FCSTD DOCUMENT  (FreeCAD 0.17R8360 (Git))
Label: cable_chain_sketch
License: All rights reserved
LicenseURL: http://de.wikipedia.org/wiki/Alle_Rechte_vorbehalten
objects: Sketcher::SketchObject×1
note: 1 computed .brp shape members not serialized (recipe doc carries the construction recipe); baked Part::Feature solids carry a one-line shape summary decoded from their .brp

FEATURE [Sketcher::SketchObject] sketch
  sketch-geometry (4):
    g0: ArcOfCircle CenterX=0 CenterY=0 CenterZ=0 NormalX=0 NormalY=0 NormalZ=1 Radius=2.5 StartAngle=1.5708 EndAngle=4.71239
    g1: ArcOfCircle CenterX=15 CenterY=0 CenterZ=0 NormalX=0 NormalY=0 NormalZ=1 Radius=2.5 StartAngle=4.71239 EndAngle=7.85398
    g2: LineSegment StartX=-7.07e-09 StartY=2.5 StartZ=0 EndX=15 EndY=2.5 EndZ=0
    g3: LineSegment StartX=0 StartY=-2.5 StartZ=0 EndX=15 EndY=-2.5 EndZ=0
  constraints (13):
    c: Coincident(g0,g-1)
    c: PointOnObject(g0,g-2)
    c: PointOnObject(g1,g-1)
    c: Coincident(g2,g0)
    c: Coincident(g2,g1)
    c: Horizontal(g2)
    c: Coincident(g3,g0)
    c: Coincident(g3,g1)
    c: Horizontal(g3)
    c: Tangent(g0,g2)
    c: Tangent(g2,g1)
    c: DistanceY(g0,g0) = 5  'H'
    c: DistanceX(g-1,g1) = 15  'L'
